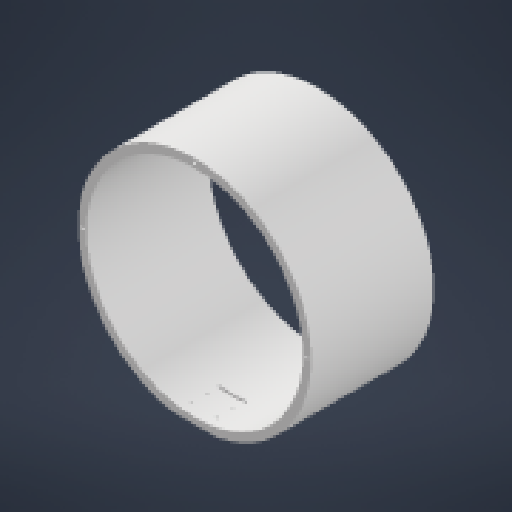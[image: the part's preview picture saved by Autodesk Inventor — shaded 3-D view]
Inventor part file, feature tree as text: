
AUTODESK INVENTOR PART (.ipt)
format: ipt  version: 2023 (Build 270158000, 158)  size: 437,760 bytes
history: native  units: mm
features: extrude x7, sketch x7
ambient origin geometry x8: Origin, YZ Plane, XZ Plane, XY Plane, X Axis, Y Axis, Z Axis, Center Point
bodies: Solid1 (feature_tree)
feature tree (14):
  extrude  "Extrusion1"  Depth=7.0mm
  extrude  "Extrusion2"  Depth=3.0mm
  extrude  "Extrusion3"  Depth=3.0mm
  extrude  "Extrusion4"  Depth=100.0mm TaperAngle=0.0deg
  extrude  "Extrusion5"  Depth=1.5mm TaperAngle=0.0deg
  extrude  "Extrusion6"  TaperAngle=180.0deg  [1 undecoded]
  extrude  "Extrusion7"  TaperAngle=90.0deg  [1 undecoded]
  sketch  "Sketch1"  dims[d0=190.0mm d3=7.0mm]
  sketch  "Sketch2"  dims[d5=3.0mm d6=3.0mm]
  sketch  "Sketch3"  dims[d7=3.0mm d8=3.0mm]
  sketch  "Sketch4"  dims[d9=100.0mm d10=0.0mm d12=100.0mm d13=0.0mm]
  sketch  "Sketch5"  dims[d14=8.0mm d15=135.0deg d16=1.5mm d17=0.0mm]
  sketch  "Sketch6"  dims[d20=12.0mm d21=180.0deg]
  sketch  "Sketch7"  dims[d22=2.0mm d23=90.0deg d24=24.0mm d25=90.0deg d26=15.0mm d27=0.0mm d28=2.0mm d30=15.0mm d31=0.0mm d32=20.0mm d33=150.0mm d34=0.0mm d35=3.0mm d37=3.0mm d39=10.0mm d40=150.0mm d41=0.0mm d42=4.982mm d43=90.0deg]
note: 2 required parameter values undecoded (feature->parameter linkage not recoverable at this tier; creation-order binding heuristic only, values carry confidence <= 0.55)
